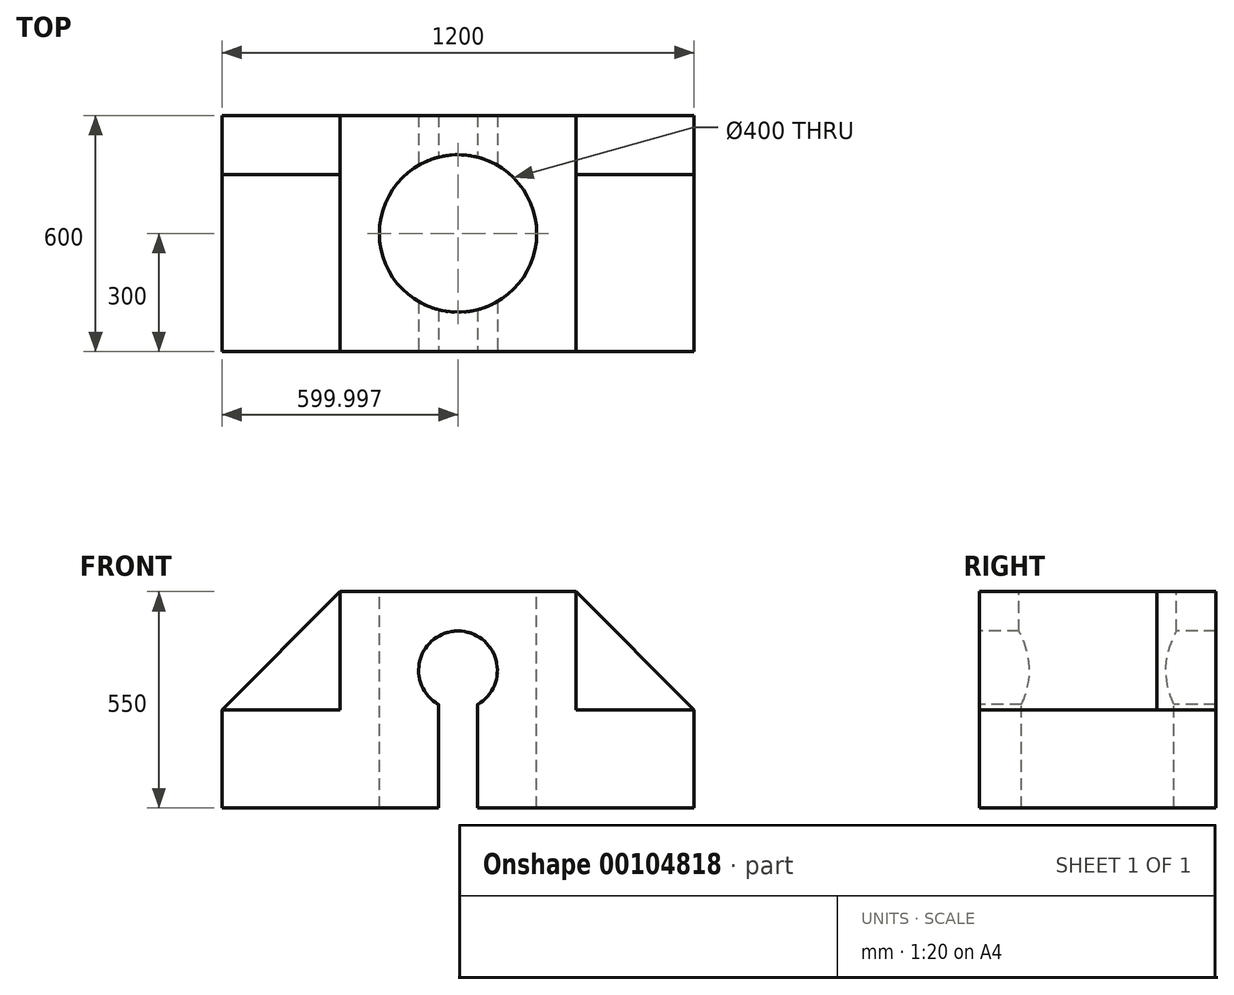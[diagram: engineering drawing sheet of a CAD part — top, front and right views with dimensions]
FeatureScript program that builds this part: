
annotation { "Feature Type Name" : "Feature", "Feature Type Description" : "" }
export const myFeature = defineFeature(function(context is Context, id is Id, definition is map)
    precondition{}
    {
        {
            var Q0;
            Q0=qCreatedBy(makeId("Front.planeOp"),FACE);
            var sketch = newSketch(context, id + "F0", { "sketchPlane" : qUnion([Q0])});
            skPoint(sketch, "E0.middle", {"position": v(0, 0) * mm});
            skPoint(sketch, "E1.start.orphan", {"position": v(0, -46.45) * mm});
            skLineSegment(sketch, "E2", {"start": v(302.48, 794.57) * mm, "end": v(1502.48, 794.57) * mm});
            skLineSegment(sketch, "E3", {"start": v(302.48, 794.57) * mm, "end": v(302.48, 1044.57) * mm});
            skLineSegment(sketch, "E4", {"start": v(1502.48, 794.57) * mm, "end": v(1502.48, 1044.57) * mm});
            skLineSegment(sketch, "E5", {"start": v(1502.48, 1044.57) * mm, "end": v(1202.48, 1044.57) * mm});
            skLineSegment(sketch, "E6", {"start": v(302.48, 1044.57) * mm, "end": v(602.48, 1044.57) * mm});
            skLineSegment(sketch, "E7", {"start": v(602.48, 1044.57) * mm, "end": v(602.48, 1344.57) * mm});
            skLineSegment(sketch, "E8", {"start": v(1202.48, 1044.57) * mm, "end": v(1202.48, 1344.57) * mm});
            skLineSegment(sketch, "E9", {"start": v(602.48, 1344.57) * mm, "end": v(1202.48, 1344.57) * mm});
            skSolve(sketch);
        }
        {
            var Q0;
            Q0 = qSketchRegion(id + "F0", true);
            extrude(context, id + "F1", {"entities" : qUnion([Q0]), "depth" : 600 * mm});
        }
        {
            var Q0;
            Q0=makeQuery(id+"F1.opExtrude","CAP_FACE",FACE,{"disambiguationData":[OSD([sQuery(id+"F0.wireOp",EDGE,"E2"),sQuery(id+"F0.wireOp",EDGE,"E3"),sQuery(id+"F0.wireOp",EDGE,"E4"),sQuery(id+"F0.wireOp",EDGE,"E5"),sQuery(id+"F0.wireOp",EDGE,"E6"),sQuery(id+"F0.wireOp",EDGE,"E7"),sQuery(id+"F0.wireOp",EDGE,"E8"),sQuery(id+"F0.wireOp",EDGE,"E9")])],"isStart":true});
            var sketch = newSketch(context, id + "F2", { "sketchPlane" : qUnion([Q0])});
            skLineSegment(sketch, "E10", {"start": v(-1502.48, 1044.57) * mm, "end": v(-1202.48, 1044.57) * mm});
            skLineSegment(sketch, "E11", {"start": v(-1202.48, 1044.57) * mm, "end": v(-1202.48, 1344.57) * mm});
            skLineSegment(sketch, "E12", {"start": v(-1202.48, 1344.57) * mm, "end": v(-1502.48, 1044.57) * mm});
            skLineSegment(sketch, "E13", {"start": v(-602.48, 1344.57) * mm, "end": v(-602.48, 1044.57) * mm});
            skLineSegment(sketch, "E14", {"start": v(-602.48, 1044.57) * mm, "end": v(-302.48, 1044.57) * mm});
            skLineSegment(sketch, "E15", {"start": v(-302.48, 1044.57) * mm, "end": v(-602.48, 1344.57) * mm});
            skSolve(sketch);
        }
        {
            var Q0;
            Q0 = qSketchRegion(id + "F2", true);
            extrude(context, id + "F3", {"entities" : qUnion([Q0]), "operationType" : NewBodyOperationType.ADD, "oppositeDirection" : true, "depth" : 150 * mm});
        }
        {
            var Q0;
            Q0=makeQuery(id+"F1.opExtrude","CAP_FACE",FACE,{"disambiguationData":[OSD([sQuery(id+"F0.wireOp",EDGE,"E2"),sQuery(id+"F0.wireOp",EDGE,"E3"),sQuery(id+"F0.wireOp",EDGE,"E4"),sQuery(id+"F0.wireOp",EDGE,"E5"),sQuery(id+"F0.wireOp",EDGE,"E6"),sQuery(id+"F0.wireOp",EDGE,"E7"),sQuery(id+"F0.wireOp",EDGE,"E8"),sQuery(id+"F0.wireOp",EDGE,"E9")])],"isStart":false});
            var sketch = newSketch(context, id + "F4", { "sketchPlane" : qUnion([Q0])});
            skArc(sketch, "E16", {"start": v(952.48, 1057.97) * mm, "mid": v(902.48, 1244.57) * mm, "end": v(852.48, 1057.97) * mm});
            skPoint(sketch, "E16.centerSnap0", {"position": v(902.48, 794.57) * mm});
            skLineSegment(sketch, "E17.top", {"start": v(952.48, 445.36) * mm, "end": v(852.48, 445.36) * mm});
            skLineSegment(sketch, "E17.left", {"start": v(952.48, 1057.97) * mm, "end": v(952.48, 445.36) * mm});
            skLineSegment(sketch, "E17.right", {"start": v(852.48, 1057.97) * mm, "end": v(852.48, 445.36) * mm});
            skPoint(sketch, "E17.bottom.start.orphan", {"position": v(952.48, 1143.77) * mm});
            skPoint(sketch, "E18.orphan", {"position": v(852.48, 1143.77) * mm});
            skSolve(sketch);
        }
        {
            var Q0;
            Q0 = qSketchRegion(id + "F4", true);
            extrude(context, id + "F5", {"entities" : qUnion([Q0]), "operationType" : NewBodyOperationType.REMOVE, "endBound" : BoundingType.THROUGH_ALL, "oppositeDirection" : true, "depth" : 25 * mm});
        }
        {
            var Q0;
            Q0=makeQuery(id+"F1.opExtrude","SWEPT_FACE",FACE,{"disambiguationData":[OSD([sQuery(id+"F0.wireOp",EDGE,"E9")])]});
            var sketch = newSketch(context, id + "F6", { "sketchPlane" : qUnion([Q0])});
            skPoint(sketch, "E19.centerSnap1", {"position": v(902.48, 0) * mm});
            skPoint(sketch, "E20", {"position": v(902.48, -300) * mm});
            skCircle(sketch, "E21", {"center": v(902.48, -300) * mm, "radius": 200 * mm});
            skSolve(sketch);
        }
        {
            var Q0;
            Q0 = qSketchRegion(id + "F6", true);
            extrude(context, id + "F7", {"entities" : qUnion([Q0]), "operationType" : NewBodyOperationType.REMOVE, "endBound" : BoundingType.THROUGH_ALL, "oppositeDirection" : true, "depth" : 25 * mm});
        }
    });
